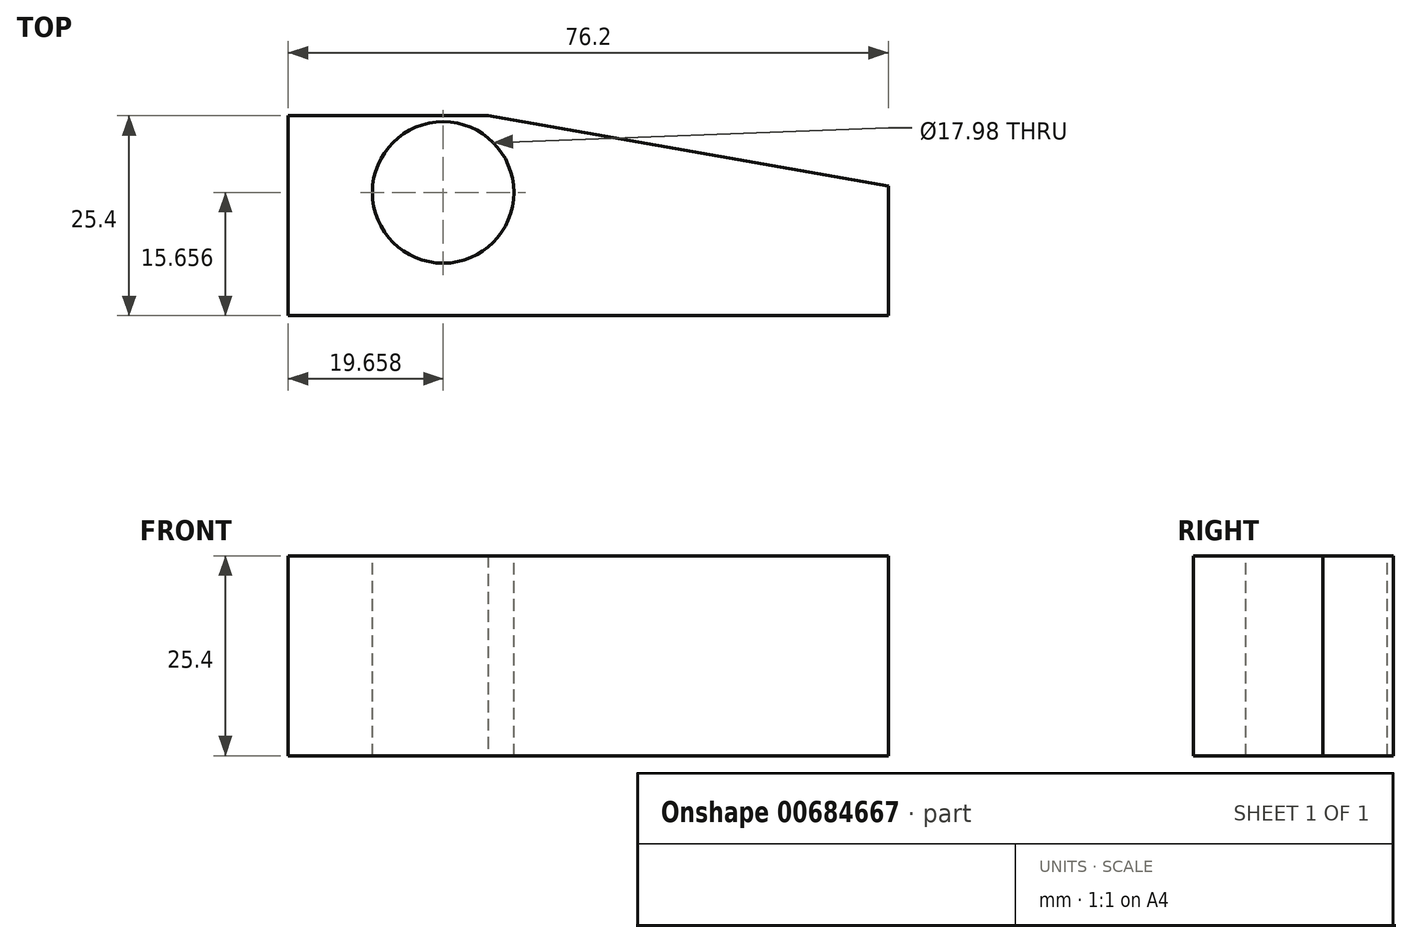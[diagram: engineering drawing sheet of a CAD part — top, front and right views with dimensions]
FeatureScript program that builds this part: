
annotation { "Feature Type Name" : "Feature", "Feature Type Description" : "" }
export const myFeature = defineFeature(function(context is Context, id is Id, definition is map)
    precondition{}
    {
        {
            var Q0;
            Q0=qCreatedBy(makeId("Top.planeOp"),FACE);
            var sketch = newSketch(context, id + "F0", { "sketchPlane" : qUnion([Q0])});
            skLineSegment(sketch, "E0.bottom", {"start": v(0, 0) * mm, "end": v(76.2, 0) * mm});
            skLineSegment(sketch, "E0.top", {"start": v(0, 25.4) * mm, "end": v(76.2, 25.4) * mm});
            skLineSegment(sketch, "E0.left", {"start": v(0, 0) * mm, "end": v(0, 25.4) * mm});
            skLineSegment(sketch, "E0.right", {"start": v(76.2, 0) * mm, "end": v(76.2, 25.4) * mm});
            skLineSegment(sketch, "E1", {"start": v(25.4, 25.4) * mm, "end": v(76.2, 16.44) * mm});
            skSolve(sketch);
        }
        {
            var Q0;
            {var subQ1=sQuery(id+"F0.wireOp",EDGE,"E0.bottom");Q0=makeQuery(id+"F0.imprint","IMPRINT",FACE,{"disambiguationData":[TD([[makeQuery(id+"F0.imprint","IMPRINT",EDGE,{"derivedFrom":subQ1}),1.0]])]});}
            extrude(context, id + "F1", {"entities" : qUnion([Q0]), "depth" : 25.4 * mm, "offsetDistance" : 25.4 * mm});
        }
        {
            var Q0;
            Q0=makeQuery(id+"F1.opExtrude","CAP_FACE",FACE,{"disambiguationData":[OSD([sQuery(id+"F0.wireOp",EDGE,"E0.bottom"),sQuery(id+"F0.wireOp",EDGE,"E0.top"),sQuery(id+"F0.wireOp",EDGE,"E0.left"),sQuery(id+"F0.wireOp",EDGE,"E0.right"),sQuery(id+"F0.wireOp",EDGE,"E1")])],"isStart":false});
            var sketch = newSketch(context, id + "F2", { "sketchPlane" : qUnion([Q0])});
            skCircle(sketch, "E2", {"center": v(19.66, 15.66) * mm, "radius": 8.99 * mm});
            skSolve(sketch);
        }
        {
            var Q0;
            Q0=makeQuery(id+"F2.imprint","IMPRINT",FACE,{"disambiguationData":[TD([[makeQuery(id+"F2.imprint","IMPRINT",EDGE,{"derivedFrom":sQuery(id+"F2.wireOp",EDGE,"E2")}),1.0]])]});
            extrude(context, id + "F3", {"entities" : qUnion([Q0]), "operationType" : NewBodyOperationType.REMOVE, "oppositeDirection" : true, "depth" : 84.84 * mm, "offsetDistance" : 25.4 * mm});
        }
    });
